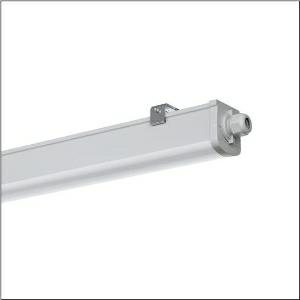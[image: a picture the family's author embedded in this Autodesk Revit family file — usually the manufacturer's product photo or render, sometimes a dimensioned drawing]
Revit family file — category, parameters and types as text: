
# Revit family: monsun_r__31_51fa20dk450b_5819
name_source: partatom
category: Lighting Fixtures
units: mm (PartAtom-declared; Revit-internal decimal feet)

## family parameters
Cut with Voids When Loaded = No
Host = Face
Light Source = No
Part Type = Normal
Room Calculation Point = No
Round Connector Dimension = Use Diameter
Shared = No

## types (1)
- Monsun® 31 (1 x LED, 5100 lm, 38 W, 4000K)
    Apparent Load = 38 VA
    CIE Flux Codes = 42 72 91 92 100
    Color Rendering = 80
    Color Temperature = 4000K
    Default Elevation = 1800 mm
    Description = Monsun® 31, damp-proof luminaire, primary optical cover: diffuser, of PC, frosted, light emission: direct distribution, primary light characteristic: symmetric, installation type: surface-mounted, LED, rated luminous flux: 5.100lm, luminous efficacy: 134lm/W, light colour: 840, colour temperature: 4000K, control gear: DALI 2, with terminal, 5+1-pole, max. 2.5mm², through-wiring: 3x 2.5mm² + 3x 1.5mm², mains connection: 220..240V, AC, 50/60Hz, rated input power: 38W, housing, luminaire housing, of PC, light grey (RAL 7035), length: 1.158mm, width: 68mm, height: 76mm, protection rating (complete): IP66, insulation class (complete): insulation class II (safety insulation), certification: CE, ENEC, UKCA, protection symbol: D, impact resistance: IK08, permissible operating ambient temperature: -20..+40°C, corresponds to IFS (International Featured Standards) requirements for safety and quality in the food industry, contact your sales advisor before using the luminaires in applications with unclear chemical exposure, large temperature fluctuations or condensation-forming humidity, packaging unit: 1 piece
    Height = 77 mm
    Lamp = 1 x LED
    Lamp Light Flux = 5100 lm
    Lamp Power = 38 W
    Lamp count = 1
    Length = 1218 mm
    Luminous efficacy = 134 lm/W
    Manufacturer = Siteco
    ModVariant = No
    Model = 51FA20DK450B
    Mounting Place = Ceiling
    Mounting Type = Surface mounted
    Number of Poles = 1
    OnlyDefault = Yes
    Power Factor = 1
    Product Name = Monsun® 31
    Product group = damp-proof luminaire
    ProductGroupID = 301
    Protection Class = Protection class II
    Protection Degree = IP 66
    RLX_Detail_Level = 1
    RLX_Emergency_Light_Flux = 0 lm
    RLX_Emergency_Type = 0
    RLX_Emergency_Type_DB = No
    RlxData = <blob elided: 33009 chars, md5=4946f782>
    Socket = socket
    Standby Power = 0 W
    System Light Flux = 5100 lm
    System Power = 38 W
    Type Comments = Product without accessories
    Type Image = l_1006174.jpg
    URL = http://relux.com
    VarID = ---
    Voltage = 0 V
    Weight = 0.00 kg
    Width = 69 mm

## geometry (parser evidence)
native form markers: Blend x4, Sweep x14
no freeform markers — native parametric forms only
